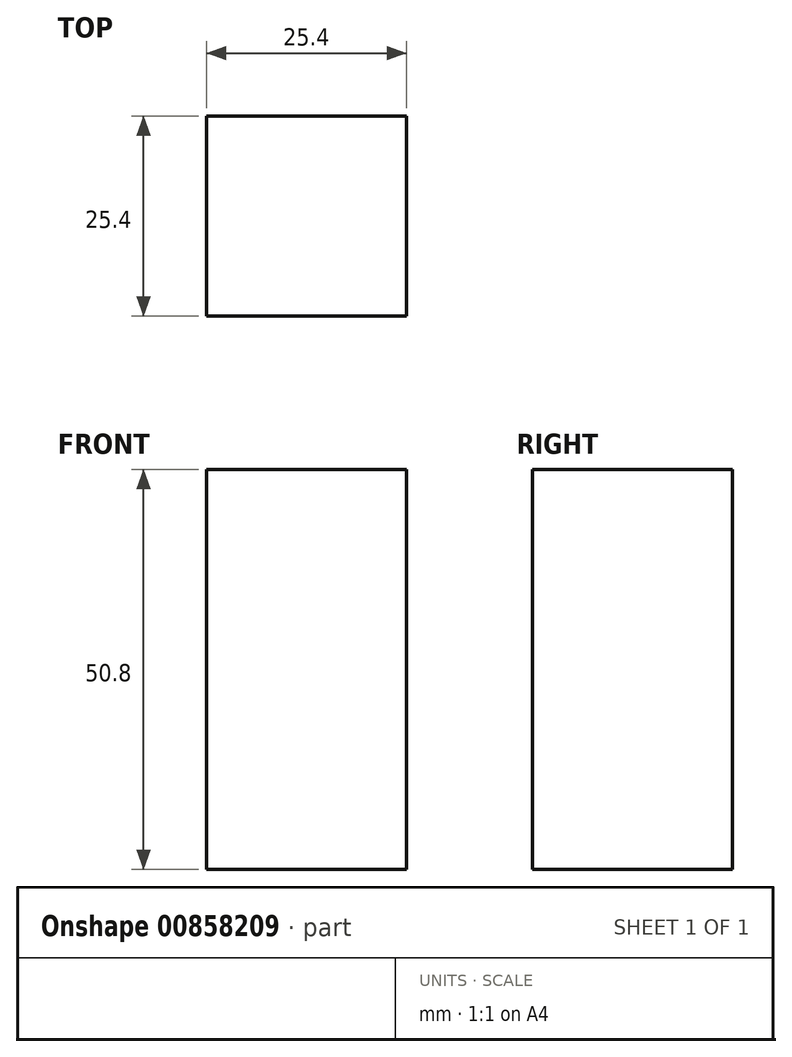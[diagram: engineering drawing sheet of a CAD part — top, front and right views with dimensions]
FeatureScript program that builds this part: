
annotation { "Feature Type Name" : "Feature", "Feature Type Description" : "" }
export const myFeature = defineFeature(function(context is Context, id is Id, definition is map)
    precondition{}
    {
        {
            var Q0;
            Q0=qCreatedBy(makeId("Top.planeOp"),FACE);
            var sketch = newSketch(context, id + "F0", { "sketchPlane" : qUnion([Q0])});
            skLineSegment(sketch, "E0.bottom", {"start": v(-12.7, 12.7) * mm, "end": v(12.7, 12.7) * mm});
            skLineSegment(sketch, "E0.top", {"start": v(-12.7, -12.7) * mm, "end": v(12.7, -12.7) * mm});
            skLineSegment(sketch, "E0.left", {"start": v(-12.7, 12.7) * mm, "end": v(-12.7, -12.7) * mm});
            skLineSegment(sketch, "E0.right", {"start": v(12.7, 12.7) * mm, "end": v(12.7, -12.7) * mm});
            skPoint(sketch, "E0.middle", {"position": v(0, 0) * mm});
            skSolve(sketch);
        }
        {
            var Q0;
            Q0 = qSketchRegion(id + "F0", true);
            extrude(context, id + "F1", {"entities" : qUnion([Q0]), "depth" : 50.8 * mm, "offsetDistance" : 25.4 * mm});
        }
    });
